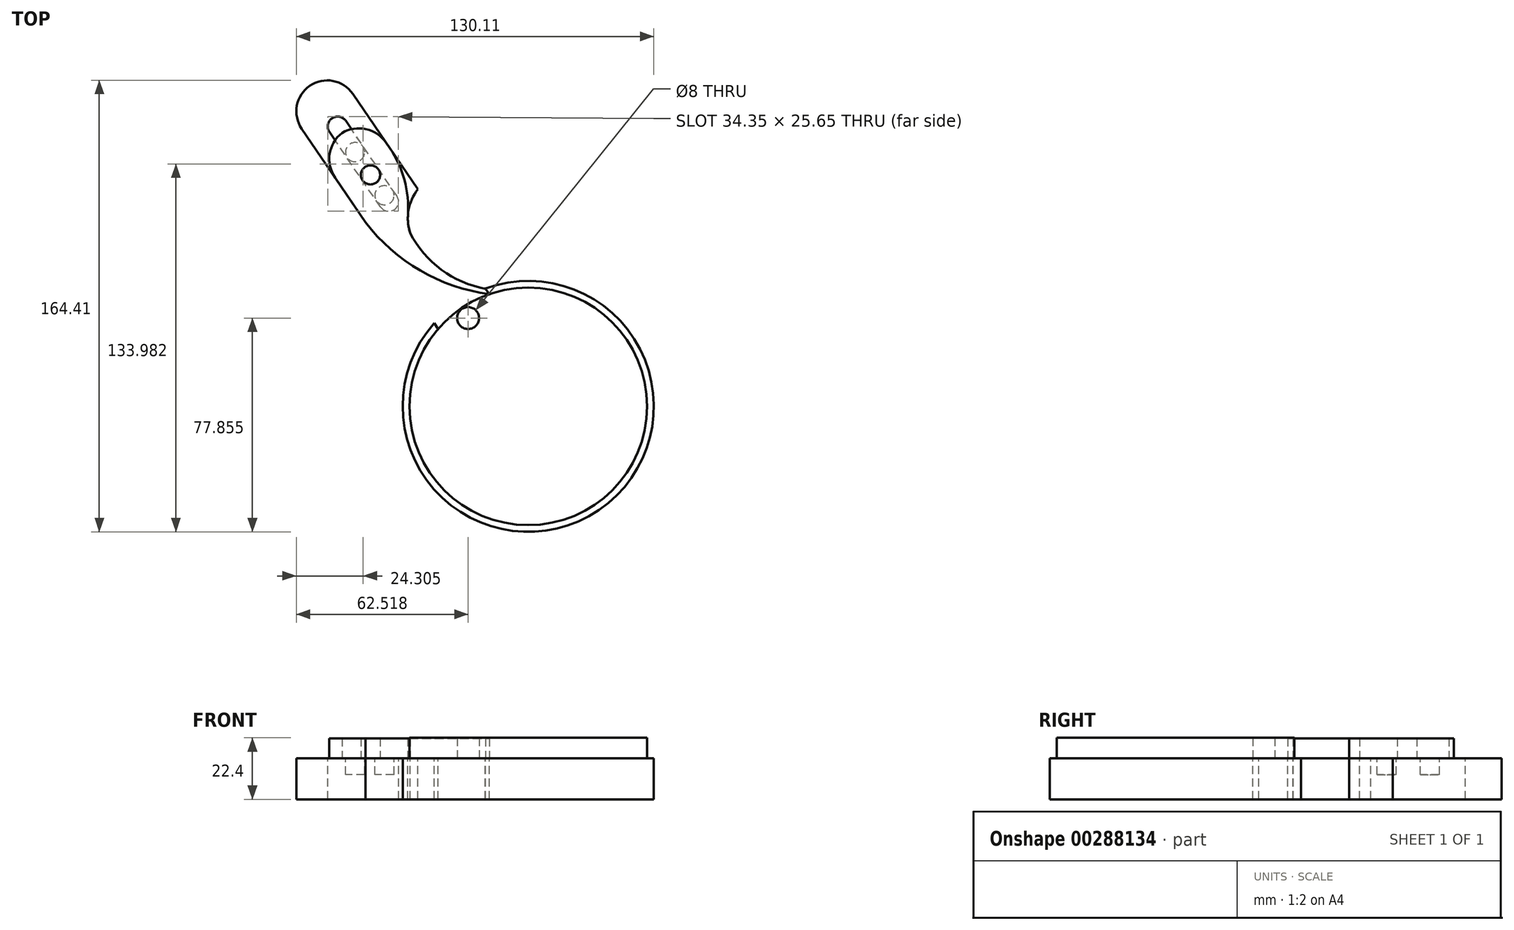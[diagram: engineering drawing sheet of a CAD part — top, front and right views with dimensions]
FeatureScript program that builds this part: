
annotation { "Feature Type Name" : "Feature", "Feature Type Description" : "" }
export const myFeature = defineFeature(function(context is Context, id is Id, definition is map)
    precondition{}
    {
        {
            var Q0;
            Q0=qCreatedBy(makeId("Top.planeOp"),FACE);
            var sketch = newSketch(context, id + "F0", { "sketchPlane" : qUnion([Q0])});
            skArc(sketch, "E0", {"start": v(-34.23, 30.28) * mm, "mid": v(25.72, -37.78) * mm, "end": v(-15.63, 42.94) * mm});
            skLineSegment(sketch, "E1.0", {"start": v(-34.23, 30.28) * mm, "end": v(-82.46, 101.13) * mm});
            skLineSegment(sketch, "E2.0", {"start": v(-15.63, 42.94) * mm, "end": v(-63.86, 113.8) * mm});
            skArc(sketch, "E3.0.startCap", {"start": v(-47.84, 76.67) * mm, "mid": v(-48.8, 71.67) * mm, "end": v(-53.8, 72.62) * mm});
            skArc(sketch, "E3.0.endCap", {"start": v(-72.37, 99.9) * mm, "mid": v(-71.42, 104.9) * mm, "end": v(-66.41, 103.95) * mm});
            skLineSegment(sketch, "E3.0.left", {"start": v(-53.8, 72.62) * mm, "end": v(-72.37, 99.9) * mm});
            skLineSegment(sketch, "E3.0.right", {"start": v(-47.84, 76.67) * mm, "end": v(-66.41, 103.95) * mm});
            skArc(sketch, "E4", {"start": v(-63.86, 113.8) * mm, "mid": v(-79.5, 116.76) * mm, "end": v(-82.46, 101.13) * mm});
            skLineSegment(sketch, "E5", {"start": v(-69.4, 101.92) * mm, "end": v(-11.46, 16.83) * mm, "construction": true});
            skSolve(sketch);
        }
        {
            var Q0;
            Q0=makeQuery(id+"F0.imprint","IMPRINT",FACE,{"disambiguationData":[TD([[makeQuery(id+"F0.imprint","IMPRINT",EDGE,{"derivedFrom":sQuery(id+"F0.wireOp",EDGE,"E0")}),1.0]])]});
            extrude(context, id + "F1", {"entities" : qUnion([Q0]), "oppositeDirection" : true, "depth" : 15 * mm});
        }
        {
            var Q0;
            Q0=qCreatedBy(makeId("Top.planeOp"),FACE);
            var sketch = newSketch(context, id + "F2", { "sketchPlane" : qUnion([Q0])});
            skCircle(sketch, "E6", {"center": v(0, 0) * mm, "radius": 43.25 * mm});
            skLineSegment(sketch, "E7.0", {"start": v(-69.4, 101.92) * mm, "end": v(-11.46, 16.83) * mm});
            skCircle(sketch, "E8", {"center": v(-21.9, 32.16) * mm, "radius": 4 * mm});
            skArc(sketch, "E9.0", {"start": v(-47.84, 76.67) * mm, "mid": v(-48.8, 71.67) * mm, "end": v(-53.8, 72.62) * mm});
            skSolve(sketch);
        }
        {
            var Q0;
            Q0=makeQuery(id+"F2.imprint","IMPRINT",FACE,{"disambiguationData":[TD([[makeQuery(id+"F2.imprint","IMPRINT",EDGE,{"derivedFrom":sQuery(id+"F2.wireOp",EDGE,"E6")}),1.0]])]});
            extrude(context, id + "F3", {"entities" : qUnion([Q0]), "depth" : 7.4 * mm});
        }
        {
            var Q0;
            Q0=qCreatedBy(makeId("Top.planeOp"),FACE);
            var sketch = newSketch(context, id + "F4", { "sketchPlane" : qUnion([Q0])});
            skLineSegment(sketch, "E10.0", {"start": v(-14.2, 40.85) * mm, "end": v(-51.76, 96) * mm});
            skLineSegment(sketch, "E11.0", {"start": v(-32.8, 28.19) * mm, "end": v(-70.35, 83.35) * mm});
            skCircle(sketch, "E12.0", {"center": v(0, 0) * mm, "radius": 43.25 * mm});
            skPoint(sketch, "E13.0", {"position": v(-48.8, 71.67) * mm});
            skLineSegment(sketch, "E14", {"start": v(-14.2, 40.85) * mm, "end": v(-32.8, 28.19) * mm});
            skLineSegment(sketch, "E15", {"start": v(-68.43, 99.18) * mm, "end": v(-67.19, 100.02) * mm});
            skCircle(sketch, "E16", {"center": v(-57.43, 84.3) * mm, "radius": 3.5 * mm});
            skPoint(sketch, "E17.orphan", {"position": v(-47.84, 76.67) * mm});
            skPoint(sketch, "E18.orphan", {"position": v(-53.8, 72.62) * mm});
            skLineSegment(sketch, "E19.0", {"start": v(-69.4, 101.92) * mm, "end": v(-11.46, 16.83) * mm, "construction": true});
            skCircle(sketch, "E20", {"center": v(-52.34, 76.87) * mm, "radius": 3.5 * mm});
            skCircle(sketch, "E21", {"center": v(-63.03, 92.58) * mm, "radius": 3.5 * mm});
            skArc(sketch, "E22", {"start": v(-59.23, 67) * mm, "mid": v(-39.3, 49.48) * mm, "end": v(-14.2, 40.85) * mm});
            skArc(sketch, "E23", {"start": v(-43, 63.15) * mm, "mid": v(-31.63, 49.79) * mm, "end": v(-15.54, 42.8) * mm});
            skArc(sketch, "E24", {"start": v(-40.2, 79.04) * mm, "mid": v(-43.56, 71.44) * mm, "end": v(-43, 63.15) * mm});
            skPoint(sketch, "E25.visualSharp", {"position": v(-58.5, 105.93) * mm});
            skArc(sketch, "E25.filletArc", {"start": v(-51.76, 96) * mm, "mid": v(-59.44, 101.05) * mm, "end": v(-68.43, 99.18) * mm});
            skPoint(sketch, "E26.visualSharp", {"position": v(-77.1, 93.27) * mm});
            skArc(sketch, "E26.filletArc", {"start": v(-67.19, 100.02) * mm, "mid": v(-72.22, 92.34) * mm, "end": v(-70.35, 83.35) * mm});
            skSolve(sketch);
        }
        {
            var Q0;
            {var subQ2=sQuery(id+"F4.wireOp",EDGE,"E10.0");Q0=makeQuery(id+"F4.imprint","IMPRINT",FACE,{"disambiguationData":[TD([[makeQuery(id+"F4.imprint","IMPRINT",EDGE,{"derivedFrom":subQ2}),1.0]])]});}
            var Q1;
            Q1=makeQuery(id+"F4.imprint","IMPRINT",FACE,{"disambiguationData":[TD([[makeQuery(id+"F4.imprint","IMPRINT",EDGE,{"derivedFrom":sQuery(id+"F4.wireOp",EDGE,"E21")}),1.0]])]});
            var Q2;
            Q2=makeQuery(id+"F4.imprint","IMPRINT",FACE,{"disambiguationData":[TD([[makeQuery(id+"F4.imprint","IMPRINT",EDGE,{"derivedFrom":sQuery(id+"F4.wireOp",EDGE,"E20")}),1.0]])]});
            extrude(context, id + "F5", {"entities" : qUnion([Q0, Q1, Q2]), "depth" : 7.2 * mm});
        }
        {
            var Q0;
            Q0=makeQuery(id+"F4.imprint","IMPRINT",FACE,{"disambiguationData":[TD([[makeQuery(id+"F4.imprint","IMPRINT",EDGE,{"derivedFrom":sQuery(id+"F4.wireOp",EDGE,"E21")}),1.0]])]});
            var Q1;
            Q1=makeQuery(id+"F4.imprint","IMPRINT",FACE,{"disambiguationData":[TD([[makeQuery(id+"F4.imprint","IMPRINT",EDGE,{"derivedFrom":sQuery(id+"F4.wireOp",EDGE,"E20")}),1.0]])]});
            extrude(context, id + "F6", {"entities" : qUnion([Q0, Q1]), "operationType" : NewBodyOperationType.ADD, "oppositeDirection" : true, "depth" : 6 * mm});
        }
        {
            var Q0;
            {var subQ4=sQuery(id+"F4.wireOp",EDGE,"E22");Q0=makeQuery(id+"F4.imprint","IMPRINT",FACE,{"disambiguationData":[TD([[makeQuery(id+"F4.imprint","IMPRINT",EDGE,{"derivedFrom":subQ4}),-1.0]])]});}
            var Q1;
            {var subQ0=sQuery(id+"F4.wireOp",EDGE,"E23");Q1=makeQuery(id+"F4.imprint","IMPRINT",FACE,{"disambiguationData":[TD([[makeQuery(id+"F4.imprint","IMPRINT",EDGE,{"derivedFrom":subQ0}),1.0]])]});}
            extrude(context, id + "F7", {"entities" : qUnion([Q0, Q1]), "operationType" : NewBodyOperationType.REMOVE, "oppositeDirection" : true, "depth" : 25 * mm});
        }
        {
            var Q0;
            Q0=makeQuery(id+"F5.opExtrude","SWEPT_EDGE",EDGE,{"disambiguationData":[OSD([sQuery(id+"F4.wireOp",EDGE,"E10.0"),sQuery(id+"F4.wireOp",EDGE,"E24")])]});
            fillet(context, id + "F8", {"entities" : qUnion([Q0]), "radius" : 38.6 * mm, "tangentPropagation" : true, "allowEdgeOverflow" : false});
        }
    });
